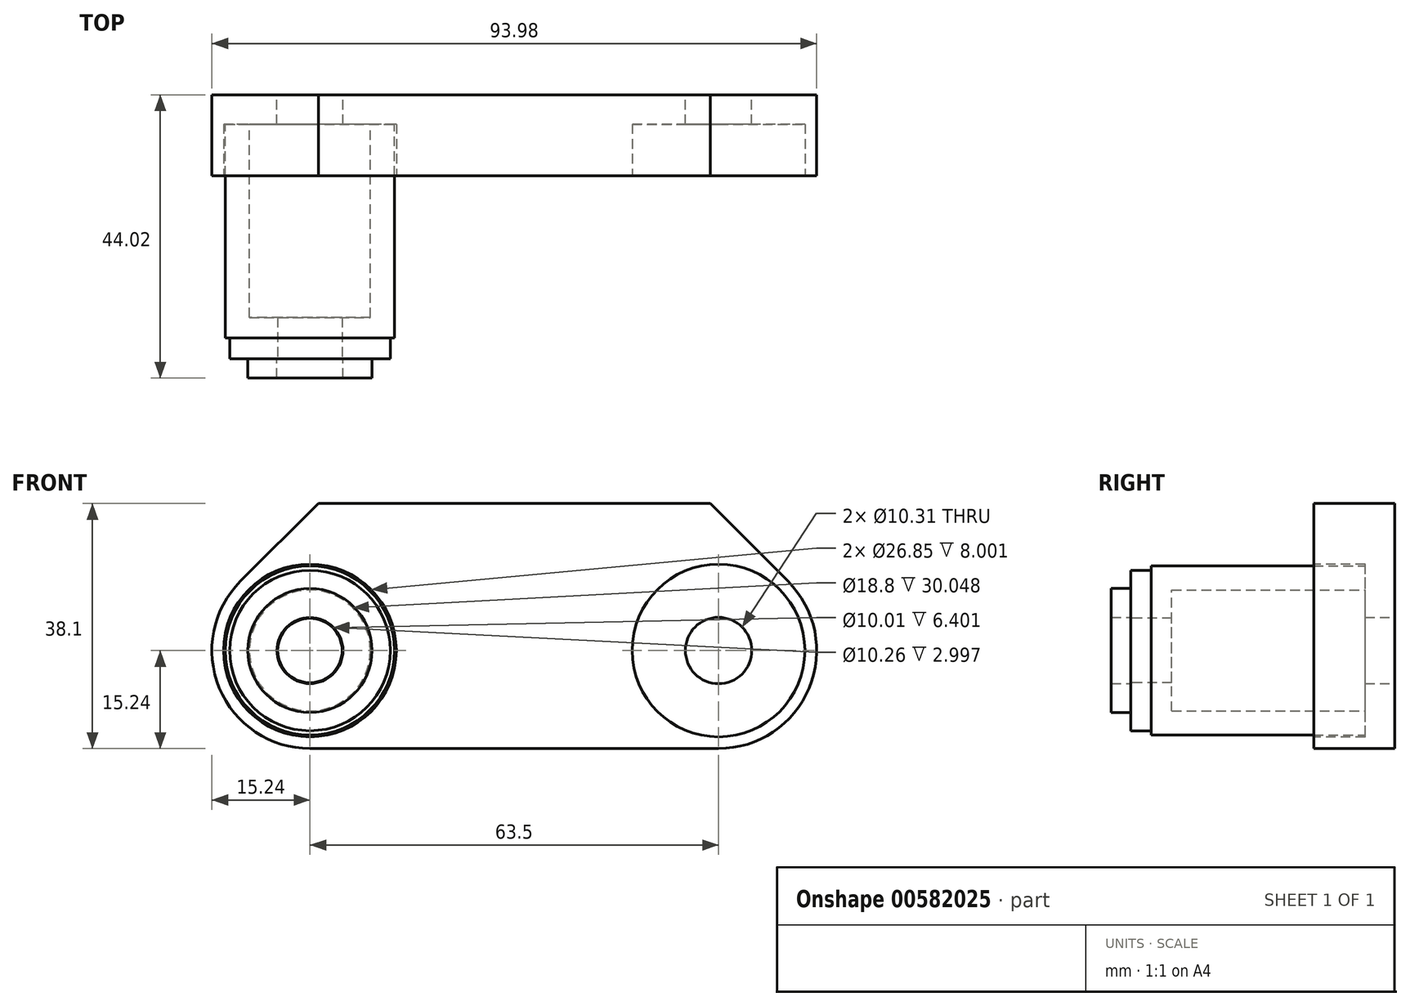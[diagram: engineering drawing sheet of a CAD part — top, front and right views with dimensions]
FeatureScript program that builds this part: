
annotation { "Feature Type Name" : "Feature", "Feature Type Description" : "" }
export const myFeature = defineFeature(function(context is Context, id is Id, definition is map)
    precondition{}
    {
        {
            var Q0;
            Q0=qCreatedBy(makeId("Front.planeOp"),FACE);
            var sketch = newSketch(context, id + "F0", { "sketchPlane" : qUnion([Q0])});
            skLineSegment(sketch, "E0", {"start": v(-31.75, 0) * mm, "end": v(31.75, 0) * mm, "construction": true});
            skArc(sketch, "E1", {"start": v(-31.75, -15.24) * mm, "mid": v(-45.83, -5.83) * mm, "end": v(-42.53, 10.78) * mm});
            skArc(sketch, "E2", {"start": v(31.75, -15.24) * mm, "mid": v(45.83, -5.83) * mm, "end": v(42.53, 10.78) * mm});
            skLineSegment(sketch, "E3", {"start": v(-31.75, -15.24) * mm, "end": v(31.75, -15.24) * mm});
            skLineSegment(sketch, "E4", {"start": v(-42.53, 10.78) * mm, "end": v(-30.44, 22.86) * mm});
            skLineSegment(sketch, "E5", {"start": v(-30.44, 22.86) * mm, "end": v(30.44, 22.86) * mm});
            skLineSegment(sketch, "E6", {"start": v(42.53, 10.78) * mm, "end": v(30.44, 22.86) * mm});
            skCircle(sketch, "E7", {"center": v(-31.75, 0) * mm, "radius": 5.16 * mm});
            skCircle(sketch, "E8", {"center": v(31.75, 0) * mm, "radius": 5.16 * mm});
            skPoint(sketch, "E9", {"position": v(-26.6, 0) * mm});
            skPoint(sketch, "E10", {"position": v(26.6, 0) * mm});
            skPoint(sketch, "E11", {"position": v(-47, 0) * mm});
            skPoint(sketch, "E12", {"position": v(47, 0) * mm});
            skSolve(sketch);
        }
        {
            var Q0;
            Q0 = qSketchRegion(id + "F0", true);
            extrude(context, id + "F1", {"entities" : qUnion([Q0]), "depth" : 12.57 * mm, "offsetDistance" : 25.4 * mm});
        }
        {
            var Q0;
            Q0=makeQuery(id+"F1.opExtrude","CAP_FACE",FACE,{"disambiguationData":[OSD([sQuery(id+"F0.wireOp",EDGE,"E1"),sQuery(id+"F0.wireOp",EDGE,"E2"),sQuery(id+"F0.wireOp",EDGE,"E3"),sQuery(id+"F0.wireOp",EDGE,"E4"),sQuery(id+"F0.wireOp",EDGE,"E5"),sQuery(id+"F0.wireOp",EDGE,"E6"),sQuery(id+"F0.wireOp",EDGE,"E7"),sQuery(id+"F0.wireOp",EDGE,"E8")])],"isStart":false});
            var sketch = newSketch(context, id + "F2", { "sketchPlane" : qUnion([Q0])});
            skCircle(sketch, "E13", {"center": v(-31.75, 0) * mm, "radius": 13.42 * mm});
            skCircle(sketch, "E14", {"center": v(31.75, 0) * mm, "radius": 13.42 * mm});
            skSolve(sketch);
        }
        {
            var Q0;
            Q0 = qSketchRegion(id + "F2", true);
            extrude(context, id + "F3", {"entities" : qUnion([Q0]), "operationType" : NewBodyOperationType.REMOVE, "oppositeDirection" : true, "depth" : 8 * mm, "offsetDistance" : 25.4 * mm});
        }
        {
            var Q0;
            Q0=makeQuery(id+"F3.boolean.opBoolean","COPY",FACE,{"derivedFrom":makeQuery(id+"F3.opExtrude","CAP_FACE",FACE,{"disambiguationData":[OSD([sQuery(id+"F2.wireOp",EDGE,"E13")])],"isStart":false})});
            var sketch = newSketch(context, id + "F4", { "sketchPlane" : qUnion([Q0])});
            skCircle(sketch, "E15", {"center": v(-31.75, 0) * mm, "radius": 13.14 * mm});
            skCircle(sketch, "E16", {"center": v(-31.75, 0) * mm, "radius": 9.4 * mm});
            skSolve(sketch);
        }
        {
            var Q0;
            Q0 = qSketchRegion(id + "F4", true);
            extrude(context, id + "F5", {"entities" : qUnion([Q0]), "depth" : 33.22 * mm, "offsetDistance" : 25.4 * mm});
        }
        {
            var Q0;
            Q0=makeQuery(id+"F5.opExtrude","CAP_FACE",FACE,{"disambiguationData":[OSD([sQuery(id+"F4.wireOp",EDGE,"E15"),sQuery(id+"F4.wireOp",EDGE,"E16")])],"isStart":false});
            var sketch = newSketch(context, id + "F6", { "sketchPlane" : qUnion([Q0])});
            skCircle(sketch, "E17", {"center": v(-31.75, 0) * mm, "radius": 9.44 * mm});
            skCircle(sketch, "E18", {"center": v(-31.75, 0) * mm, "radius": 5 * mm});
            skSolve(sketch);
        }
        {
            var Q0;
            Q0 = qSketchRegion(id + "F6", true);
            extrude(context, id + "F7", {"entities" : qUnion([Q0]), "operationType" : NewBodyOperationType.ADD, "oppositeDirection" : true, "depth" : 3.17 * mm, "offsetDistance" : 25.4 * mm});
        }
        {
            var Q0;
            Q0=makeQuery(id+"F7.opExtrude","CAP_FACE",FACE,{"disambiguationData":[OSD([sQuery(id+"F6.wireOp",EDGE,"E17"),sQuery(id+"F6.wireOp",EDGE,"E18")])],"isStart":true});
            var sketch = newSketch(context, id + "F8", { "sketchPlane" : qUnion([Q0])});
            skCircle(sketch, "E19.0", {"center": v(-31.75, 0) * mm, "radius": 5 * mm});
            skCircle(sketch, "E20", {"center": v(-31.75, 0) * mm, "radius": 12.47 * mm});
            skSolve(sketch);
        }
        {
            var Q0;
            Q0 = qSketchRegion(id + "F8", true);
            extrude(context, id + "F9", {"entities" : qUnion([Q0]), "operationType" : NewBodyOperationType.ADD, "depth" : 3.23 * mm, "offsetDistance" : 25.4 * mm});
        }
        {
            var Q0;
            Q0=makeQuery(id+"F9.opExtrude","CAP_FACE",FACE,{"disambiguationData":[OSD([sQuery(id+"F8.wireOp",EDGE,"E19.0"),sQuery(id+"F8.wireOp",EDGE,"E20")])],"isStart":false});
            var sketch = newSketch(context, id + "F10", { "sketchPlane" : qUnion([Q0])});
            skCircle(sketch, "E21", {"center": v(-31.75, 0) * mm, "radius": 9.64 * mm});
            skCircle(sketch, "E22", {"center": v(-31.75, 0) * mm, "radius": 5.13 * mm});
            skSolve(sketch);
        }
        {
            var Q0;
            Q0 = qSketchRegion(id + "F10", true);
            extrude(context, id + "F11", {"entities" : qUnion([Q0]), "operationType" : NewBodyOperationType.ADD, "depth" : 3 * mm, "offsetDistance" : 25.4 * mm});
        }
    });
